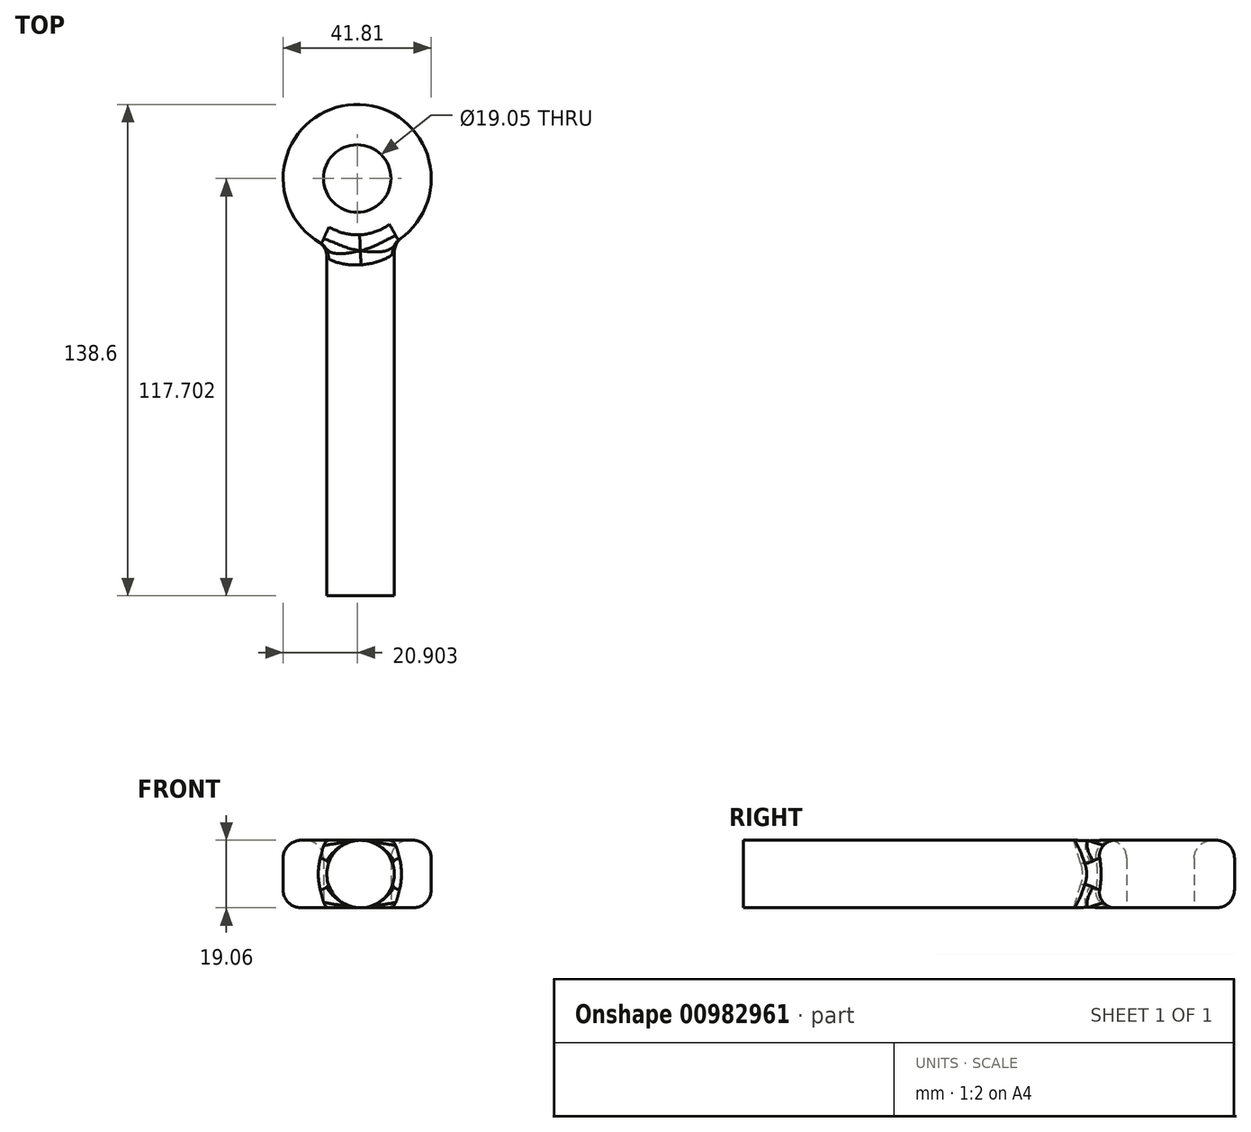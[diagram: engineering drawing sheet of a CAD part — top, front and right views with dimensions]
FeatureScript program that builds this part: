
annotation { "Feature Type Name" : "Feature", "Feature Type Description" : "" }
export const myFeature = defineFeature(function(context is Context, id is Id, definition is map)
    precondition{}
    {
        {
            var Q0;
            Q0=qCreatedBy(makeId("Front.planeOp"),FACE);
            var sketch = newSketch(context, id + "F0", { "sketchPlane" : qUnion([Q0])});
            skCircle(sketch, "E0", {"center": v(0, 0) * mm, "radius": 9.53 * mm});
            skSolve(sketch);
        }
        {
            var Q0;
            Q0 = qSketchRegion(id + "F0", true);
            extrude(context, id + "F1", {"entities" : qUnion([Q0]), "depth" : 101.6 * mm, "offsetDistance" : 25.4 * mm});
        }
        {
            var Q0;
            Q0=qCreatedBy(makeId("Top.planeOp"),FACE);
            var sketch = newSketch(context, id + "F2", { "sketchPlane" : qUnion([Q0])});
            skCircle(sketch, "E1", {"center": v(-0.95, 16.1) * mm, "radius": 20.9 * mm});
            skPoint(sketch, "E1.first.point", {"position": v(0, -4.78) * mm});
            skPoint(sketch, "E1.second.point", {"position": v(-10.41, 34.74) * mm});
            skPoint(sketch, "E1.third.point", {"position": v(8.92, 34.53) * mm});
            skCircle(sketch, "E2.0", {"center": v(-0.95, 16.1) * mm, "radius": 9.53 * mm});
            skSolve(sketch);
        }
        {
            var Q0;
            Q0 = qSketchRegion(id + "F2", true);
            extrude(context, id + "F3", {"entities" : qUnion([Q0]), "operationType" : NewBodyOperationType.ADD, "endBound" : BoundingType.SYMMETRIC, "depth" : 19.05 * mm, "offsetDistance" : 25.4 * mm});
        }
        {
            var Q0;
            Q0=makeQuery(id+"F3.opExtrude","CAP_EDGE",EDGE,{"disambiguationData":[OSD([sQuery(id+"F2.wireOp",EDGE,"E1")])],"isStart":false});
            var Q1;
            Q1=makeQuery(id+"F3.boolean.opBoolean","INTERSECT",EDGE,{"disambiguationData":[OD(1.0)],"derivedFrom":[makeQuery(id+"F1.opExtrude","SWEPT_FACE",FACE,{"disambiguationData":[OSD([sQuery(id+"F0.wireOp",EDGE,"E0")])]}),makeQuery(id+"F3.opExtrude","SWEPT_FACE",FACE,{"disambiguationData":[OSD([sQuery(id+"F2.wireOp",EDGE,"E1")])]})]});
            var Q2;
            Q2=makeQuery(id+"F3.boolean.opBoolean","INTERSECT",EDGE,{"disambiguationData":[OD(0.0)],"derivedFrom":[makeQuery(id+"F1.opExtrude","SWEPT_FACE",FACE,{"disambiguationData":[OSD([sQuery(id+"F0.wireOp",EDGE,"E0")])]}),makeQuery(id+"F3.opExtrude","SWEPT_FACE",FACE,{"disambiguationData":[OSD([sQuery(id+"F2.wireOp",EDGE,"E1")])]})]});
            var Q3;
            Q3=makeQuery(id+"F3.opExtrude","CAP_EDGE",EDGE,{"disambiguationData":[OSD([sQuery(id+"F2.wireOp",EDGE,"E1")])],"isStart":true});
            var Q4;
            Q4=makeQuery(id+"F3.opExtrude","CAP_EDGE",EDGE,{"disambiguationData":[OSD([sQuery(id+"F2.wireOp",EDGE,"E2.0")])],"isStart":false});
            fillet(context, id + "F4", {"entities" : qUnion([Q0, Q1, Q2, Q3, Q4]), "radius" : 5.08 * mm, "tangentPropagation" : true, "allowEdgeOverflow" : false});
        }
    });
